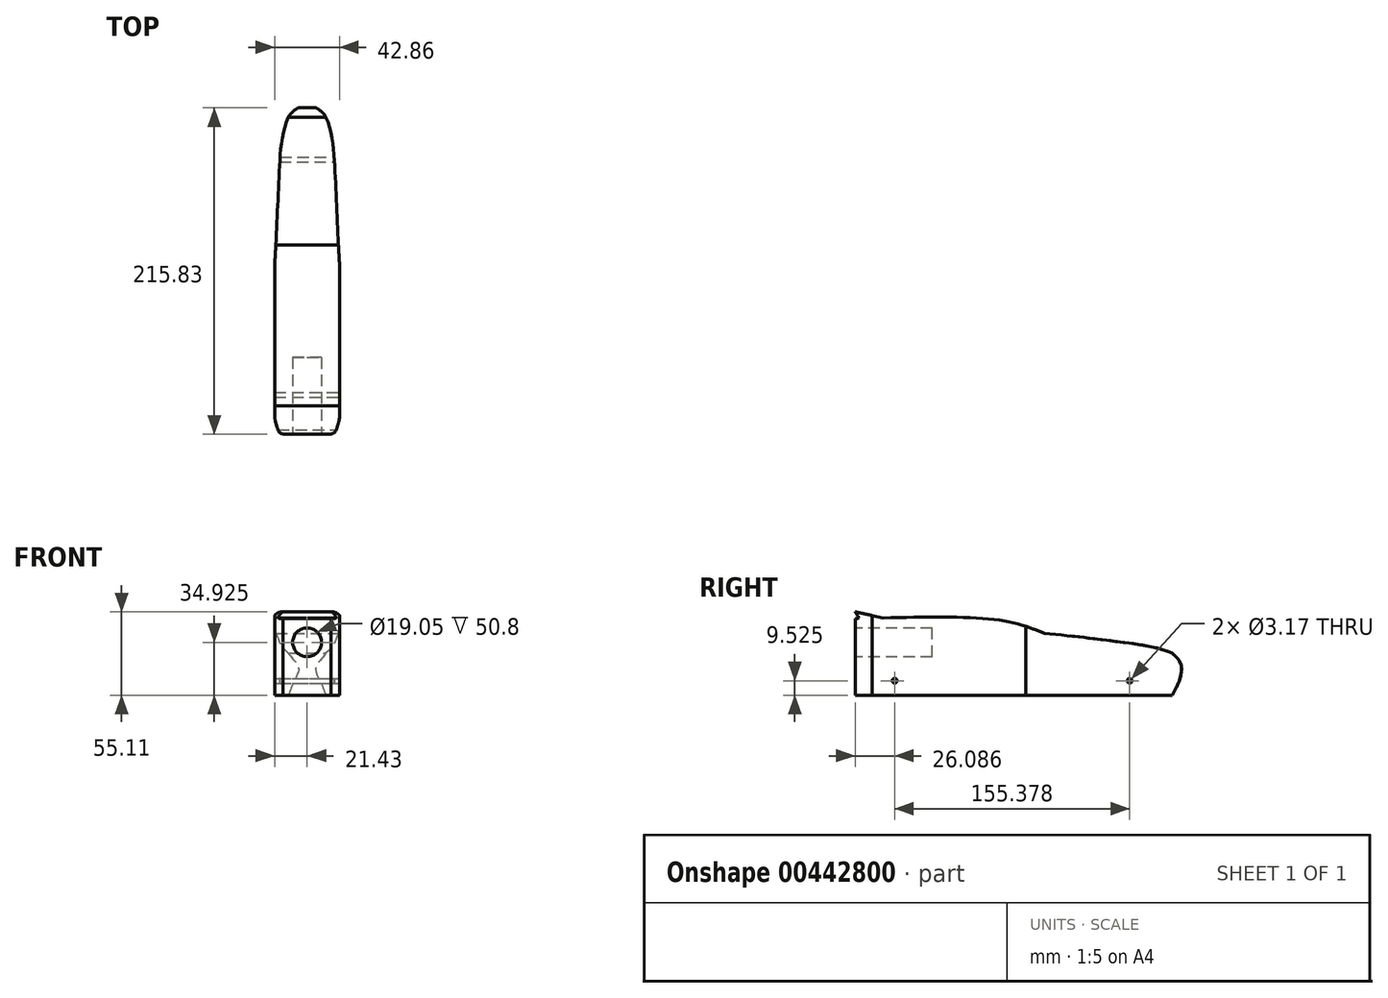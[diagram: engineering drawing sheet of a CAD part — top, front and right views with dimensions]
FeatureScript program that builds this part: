
annotation { "Feature Type Name" : "Feature", "Feature Type Description" : "" }
export const myFeature = defineFeature(function(context is Context, id is Id, definition is map)
    precondition{}
    {
        {
            var Q0;
            Q0=qCreatedBy(makeId("Right.planeOp"),FACE);
            var sketch = newSketch(context, id + "F0", { "sketchPlane" : qUnion([Q0])});
            skLineSegment(sketch, "E0", {"start": v(-152.4, 0) * mm, "end": v(152.4, 0) * mm});
            skLineSegment(sketch, "E1", {"start": v(-152.4, 0) * mm, "end": v(-152.4, 69.85) * mm});
            skLineSegment(sketch, "E2", {"start": v(152.4, 0) * mm, "end": v(152.4, 19.05) * mm});
            skLineSegment(sketch, "E3", {"start": v(152.4, 19.05) * mm, "end": v(-152.4, 69.85) * mm});
            skPoint(sketch, "E4.endSnap0", {"position": v(-152.4, 34.93) * mm});
            skLineSegment(sketch, "E5.0", {"start": v(-95.25, 50.8) * mm, "end": v(-152.4, 50.8) * mm, "construction": true});
            skLineSegment(sketch, "E5.1", {"start": v(-95.25, 50.8) * mm, "end": v(-95.25, 19.05) * mm, "construction": true});
            skLineSegment(sketch, "E5.2", {"start": v(-95.25, 19.05) * mm, "end": v(-152.4, 19.05) * mm, "construction": true});
            skSolve(sketch);
        }
        {
            var Q0;
            Q0=makeQuery(id+"F0.imprint","IMPRINT",FACE,{"disambiguationData":[TD([[makeQuery(id+"F0.imprint","IMPRINT",EDGE,{"derivedFrom":sQuery(id+"F0.wireOp",EDGE,"E0")}),1.0]])]});
            extrude(context, id + "F1", {"entities" : qUnion([Q0]), "depth" : 42.86 * mm, "symmetric" : true});
        }
        {
            var Q0;
            Q0=makeQuery(id+"F1.opExtrude","SWEPT_FACE",FACE,{"disambiguationData":[OSD([sQuery(id+"F0.wireOp",EDGE,"E1")])]});
            var sketch = newSketch(context, id + "F2", { "sketchPlane" : qUnion([Q0])});
            skLineSegment(sketch, "E6", {"start": v(21.43, 34.93) * mm, "end": v(0, 34.93) * mm, "construction": true});
            skCircle(sketch, "E7", {"center": v(0, 34.93) * mm, "radius": 9.53 * mm});
            skSolve(sketch);
        }
        {
            var Q0;
            Q0=makeQuery(id+"F2.imprint","IMPRINT",FACE,{"disambiguationData":[TD([[makeQuery(id+"F2.imprint","IMPRINT",EDGE,{"derivedFrom":sQuery(id+"F2.wireOp",EDGE,"E7")}),1.0]])]});
            var Q1;
            Q1=sQuery(id+"F2.wireOp",EDGE,"E7");
            extrude(context, id + "F3", {"entities" : qUnion([Q0]), "operationType" : NewBodyOperationType.REMOVE, "surfaceEntities" : qUnion([Q1]), "oppositeDirection" : true, "depth" : 50.8 * mm});
        }
        {
            var Q0;
            Q0=makeQuery(id+"F1.opExtrude","CAP_FACE",FACE,{"disambiguationData":[OSD([sQuery(id+"F0.wireOp",EDGE,"E0"),sQuery(id+"F0.wireOp",EDGE,"E1"),sQuery(id+"F0.wireOp",EDGE,"E2"),sQuery(id+"F0.wireOp",EDGE,"E3")])],"isStart":false});
            var sketch = newSketch(context, id + "F4", { "sketchPlane" : qUnion([Q0])});
            skLineSegment(sketch, "E8.1", {"start": v(-95.25, 50.8) * mm, "end": v(-95.25, 19.05) * mm, "construction": true});
            skLineSegment(sketch, "E8.2", {"start": v(-152.4, 50.8) * mm, "end": v(-95.25, 50.8) * mm, "construction": true});
            skLineSegment(sketch, "E9", {"start": v(-152.4, 44.45) * mm, "end": v(-101.6, 44.45) * mm, "construction": true});
            skLineSegment(sketch, "E10", {"start": v(-101.6, 44.45) * mm, "end": v(-101.6, 25.4) * mm, "construction": true});
            skLineSegment(sketch, "E11", {"start": v(-101.6, 25.4) * mm, "end": v(-152.4, 25.4) * mm, "construction": true});
            skPoint(sketch, "E12.start.orphan", {"position": v(-152.4, 34.93) * mm});
            skLineSegment(sketch, "E13", {"start": v(-95.25, 19.05) * mm, "end": v(-152.4, 19.05) * mm, "construction": true});
            skLineSegment(sketch, "E14", {"start": v(-152.4, 50.8) * mm, "end": v(-149.7, 50.84) * mm});
            skLineSegment(sketch, "E15", {"start": v(-133.82, 51.08) * mm, "end": v(-152.4, 55.1) * mm});
            skLineSegment(sketch, "E16", {"start": v(-152.4, 55.1) * mm, "end": v(-149.7, 50.84) * mm});
            skFitSpline(sketch, "E17", {"points": [v(-27.34, 40.87) * mm, v(-55.18, 49.32) * mm, v(-133.82, 51.08) * mm], "startDerivative": vector(-63.63, 26.03) * mm, "endDerivative": vector(-142.9, -3.22) * mm});
            skFitSpline(sketch, "E18", {"points": [v(-27.34, 40.87) * mm, v(25.78, 34.79) * mm, v(57.15, 27.67) * mm], "startDerivative": vector(100.66, -9.25) * mm, "endDerivative": vector(63.75, -28.42) * mm});
            skFitSpline(sketch, "E19", {"points": [v(57.15, 27.67) * mm, v(63.27, 15.05) * mm, v(57.15, 0) * mm], "startDerivative": vector(36.15, -28.1) * mm, "endDerivative": vector(-18.17, -29.76) * mm});
            skCircle(sketch, "E20", {"center": v(-126.31, 9.53) * mm, "radius": 1.59 * mm});
            skCircle(sketch, "E21", {"center": v(29.06, 9.53) * mm, "radius": 1.59 * mm});
            skSolve(sketch);
        }
        {
            var Q0;
            Q0=makeQuery(id+"F1.opExtrude","SWEPT_FACE",FACE,{"disambiguationData":[OSD([sQuery(id+"F0.wireOp",EDGE,"E0")])]});
            var sketch = newSketch(context, id + "F5", { "sketchPlane" : qUnion([Q0])});
            skLineSegment(sketch, "E22", {"start": v(0, 152.4) * mm, "end": v(0, -152.4) * mm, "construction": true});
            skLineSegment(sketch, "E23", {"start": v(15.88, 152.4) * mm, "end": v(15.88, 95.25) * mm, "construction": true});
            skLineSegment(sketch, "E24", {"start": v(15.88, 95.25) * mm, "end": v(-15.87, 95.25) * mm, "construction": true});
            skLineSegment(sketch, "E25", {"start": v(-15.87, 95.25) * mm, "end": v(-15.87, 152.4) * mm, "construction": true});
            skLineSegment(sketch, "E26", {"start": v(0, 152.4) * mm, "end": v(-9.53, 152.4) * mm, "construction": true});
            skLineSegment(sketch, "E27", {"start": v(-9.53, 152.4) * mm, "end": v(-9.53, 101.6) * mm, "construction": true});
            skLineSegment(sketch, "E28", {"start": v(-9.52, 101.6) * mm, "end": v(9.53, 101.6) * mm, "construction": true});
            skLineSegment(sketch, "E29", {"start": v(9.53, 101.6) * mm, "end": v(9.53, 152.4) * mm, "construction": true});
            skPoint(sketch, "E30.MirrorCS.start.orphan", {"position": v(21.43, 27.17) * mm});
            skPoint(sketch, "E31.MirrorCS.end.orphan", {"position": v(21.43, 152.4) * mm});
            skPoint(sketch, "E32.end.orphan", {"position": v(-21.43, 152.4) * mm});
            skLineSegment(sketch, "E33", {"start": v(-21.43, 141.33) * mm, "end": v(-21.43, 39.69) * mm});
            skFitSpline(sketch, "E34", {"points": [v(-21.43, 141.33) * mm, v(-19.76, 148.15) * mm, v(-15.87, 152.4) * mm], "startDerivative": vector(1.86, 14.06) * mm, "endDerivative": vector(18.12, 5.62) * mm});
            skFitSpline(sketch, "E35", {"points": [v(-21.43, 39.69) * mm, v(-18.14, -26.95) * mm, v(-15.29, -48.52) * mm, v(0, -64.59) * mm], "startDerivative": vector(10.29, -154.55) * mm, "endDerivative": vector(122.73, -5) * mm});
            skFitSpline(sketch, "E36.MirrorCS", {"points": [v(21.43, 39.69) * mm, v(18.14, -26.95) * mm, v(15.29, -48.52) * mm, v(0, -64.59) * mm], "startDerivative": vector(-10.29, -154.55) * mm, "endDerivative": vector(-122.73, -5) * mm});
            skLineSegment(sketch, "E37.MirrorCS", {"start": v(21.43, 141.33) * mm, "end": v(21.43, 39.69) * mm});
            skFitSpline(sketch, "E38.MirrorCS", {"points": [v(21.43, 141.33) * mm, v(19.76, 148.15) * mm, v(15.87, 152.4) * mm], "startDerivative": vector(-1.86, 14.06) * mm, "endDerivative": vector(-18.12, 5.62) * mm});
            skSolve(sketch);
        }
        {
            var Q0;
            {var subQ0=sQuery(id+"F4.wireOp",EDGE,"E14");Q0=makeQuery(id+"F4.imprint","IMPRINT",FACE,{"disambiguationData":[TD([[makeQuery(id+"F4.imprint","IMPRINT",EDGE,{"derivedFrom":subQ0}),-1.0]])]});}
            extrude(context, id + "F6", {"entities" : qUnion([Q0]), "operationType" : NewBodyOperationType.INTERSECT, "endBound" : BoundingType.THROUGH_ALL, "oppositeDirection" : true, "depth" : 25.4 * mm});
        }
        {
            var Q0;
            Q0=makeQuery(id+"F5.imprint","IMPRINT",FACE,{"disambiguationData":[TD([[makeQuery(id+"F5.imprint","IMPRINT",EDGE,{"derivedFrom":sQuery(id+"F5.wireOp",EDGE,"E33")}),1.0]])]});
            extrude(context, id + "F7", {"entities" : qUnion([Q0]), "operationType" : NewBodyOperationType.INTERSECT, "endBound" : BoundingType.THROUGH_ALL, "oppositeDirection" : true, "depth" : 25.4 * mm});
        }
    });
